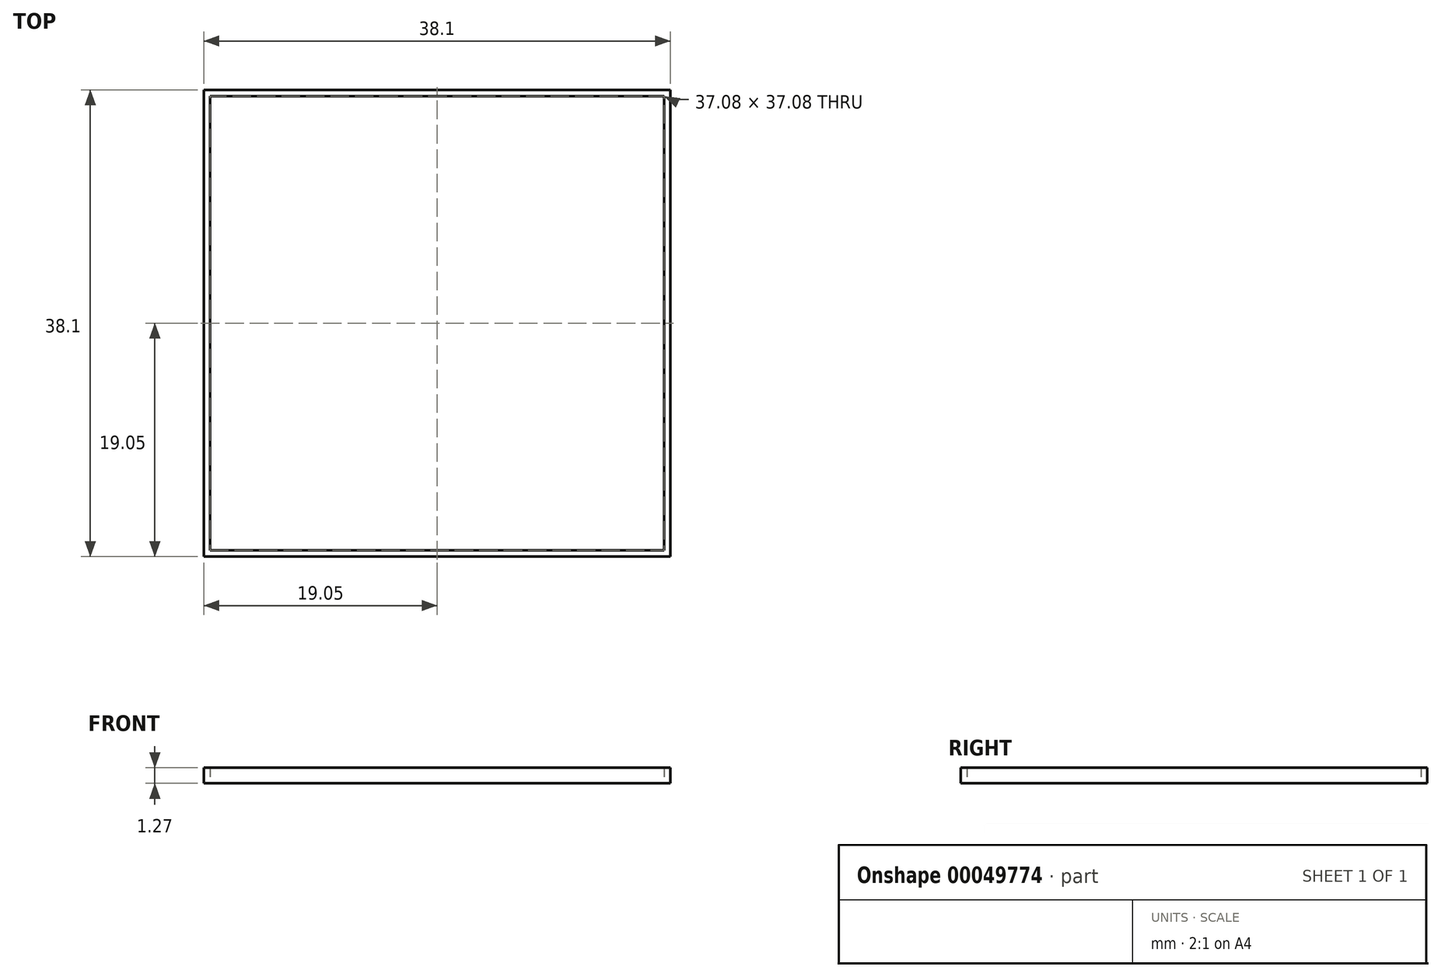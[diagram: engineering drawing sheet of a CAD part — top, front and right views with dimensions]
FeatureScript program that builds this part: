
annotation { "Feature Type Name" : "Feature", "Feature Type Description" : "" }
export const myFeature = defineFeature(function(context is Context, id is Id, definition is map)
    precondition{}
    {
        {
            var Q0;
            Q0=qCreatedBy(makeId("Top.planeOp"),FACE);
            var sketch = newSketch(context, id + "F0", { "sketchPlane" : qUnion([Q0])});
            skLineSegment(sketch, "E0.rect.bottom", {"start": v(19.05, -19.05) * mm, "end": v(-19.05, -19.05) * mm});
            skLineSegment(sketch, "E0.rect.top", {"start": v(19.05, 19.05) * mm, "end": v(-19.05, 19.05) * mm});
            skLineSegment(sketch, "E0.rect.left", {"start": v(19.05, -19.05) * mm, "end": v(19.05, 19.05) * mm});
            skLineSegment(sketch, "E0.rect.right", {"start": v(-19.05, -19.05) * mm, "end": v(-19.05, 19.05) * mm});
            skPoint(sketch, "E0.rect.middle", {"position": v(0, 0) * mm});
            skLineSegment(sketch, "E1.1.0.0", {"start": v(-18.54, -19.05) * mm, "end": v(-18.54, 19.05) * mm});
            skLineSegment(sketch, "E1.2.0.0", {"start": v(-18.03, -19.05) * mm, "end": v(-18.03, 19.05) * mm});
            skLineSegment(sketch, "E1.3.0.0", {"start": v(-17.53, -19.05) * mm, "end": v(-17.53, 19.05) * mm});
            skLineSegment(sketch, "E1.4.0.0", {"start": v(-17.02, -19.05) * mm, "end": v(-17.02, 19.05) * mm});
            skLineSegment(sketch, "E1.5.0.0", {"start": v(-16.5, -19.05) * mm, "end": v(-16.5, 19.05) * mm});
            skLineSegment(sketch, "E1.6.0.0", {"start": v(-16, -19.05) * mm, "end": v(-16, 19.05) * mm});
            skLineSegment(sketch, "E1.7.0.0", {"start": v(-15.5, -19.05) * mm, "end": v(-15.5, 19.05) * mm});
            skLineSegment(sketch, "E1.8.0.0", {"start": v(-14.99, -19.05) * mm, "end": v(-14.99, 19.05) * mm});
            skLineSegment(sketch, "E1.9.0.0", {"start": v(-14.48, -19.05) * mm, "end": v(-14.48, 19.05) * mm});
            skLineSegment(sketch, "E1.10.0.0", {"start": v(-13.97, -19.05) * mm, "end": v(-13.97, 19.05) * mm});
            skLineSegment(sketch, "E1.11.0.0", {"start": v(-13.46, -19.05) * mm, "end": v(-13.46, 19.05) * mm});
            skLineSegment(sketch, "E1.12.0.0", {"start": v(-12.95, -19.05) * mm, "end": v(-12.95, 19.05) * mm});
            skLineSegment(sketch, "E1.13.0.0", {"start": v(-12.45, -19.05) * mm, "end": v(-12.45, 19.05) * mm});
            skLineSegment(sketch, "E1.14.0.0", {"start": v(-11.94, -19.05) * mm, "end": v(-11.94, 19.05) * mm});
            skLineSegment(sketch, "E1.15.0.0", {"start": v(-11.43, -19.05) * mm, "end": v(-11.43, 19.05) * mm});
            skLineSegment(sketch, "E1.16.0.0", {"start": v(-10.92, -19.05) * mm, "end": v(-10.92, 19.05) * mm});
            skLineSegment(sketch, "E1.17.0.0", {"start": v(-10.41, -19.05) * mm, "end": v(-10.41, 19.05) * mm});
            skLineSegment(sketch, "E1.18.0.0", {"start": v(-9.9, -19.05) * mm, "end": v(-9.9, 19.05) * mm});
            skLineSegment(sketch, "E1.19.0.0", {"start": v(-9.4, -19.05) * mm, "end": v(-9.4, 19.05) * mm});
            skLineSegment(sketch, "E1.20.0.0", {"start": v(-8.89, -19.05) * mm, "end": v(-8.89, 19.05) * mm});
            skLineSegment(sketch, "E1.21.0.0", {"start": v(-8.38, -19.05) * mm, "end": v(-8.38, 19.05) * mm});
            skLineSegment(sketch, "E1.22.0.0", {"start": v(-7.87, -19.05) * mm, "end": v(-7.87, 19.05) * mm});
            skLineSegment(sketch, "E1.23.0.0", {"start": v(-7.37, -19.05) * mm, "end": v(-7.37, 19.05) * mm});
            skLineSegment(sketch, "E1.24.0.0", {"start": v(-6.86, -19.05) * mm, "end": v(-6.86, 19.05) * mm});
            skLineSegment(sketch, "E1.25.0.0", {"start": v(-6.35, -19.05) * mm, "end": v(-6.35, 19.05) * mm});
            skLineSegment(sketch, "E1.26.0.0", {"start": v(-5.84, -19.05) * mm, "end": v(-5.84, 19.05) * mm});
            skLineSegment(sketch, "E1.27.0.0", {"start": v(-5.33, -19.05) * mm, "end": v(-5.33, 19.05) * mm});
            skLineSegment(sketch, "E1.28.0.0", {"start": v(-4.83, -19.05) * mm, "end": v(-4.83, 19.05) * mm});
            skLineSegment(sketch, "E1.29.0.0", {"start": v(-4.32, -19.05) * mm, "end": v(-4.32, 19.05) * mm});
            skLineSegment(sketch, "E1.30.0.0", {"start": v(-3.8, -19.05) * mm, "end": v(-3.8, 19.05) * mm});
            skLineSegment(sketch, "E1.31.0.0", {"start": v(-3.3, -19.05) * mm, "end": v(-3.3, 19.05) * mm});
            skLineSegment(sketch, "E1.32.0.0", {"start": v(-2.8, -19.05) * mm, "end": v(-2.8, 19.05) * mm});
            skLineSegment(sketch, "E1.33.0.0", {"start": v(-2.29, -19.05) * mm, "end": v(-2.29, 19.05) * mm});
            skLineSegment(sketch, "E1.34.0.0", {"start": v(-1.78, -19.05) * mm, "end": v(-1.78, 19.05) * mm});
            skLineSegment(sketch, "E1.35.0.0", {"start": v(-1.27, -19.05) * mm, "end": v(-1.27, 19.05) * mm});
            skLineSegment(sketch, "E1.36.0.0", {"start": v(-0.76, -19.05) * mm, "end": v(-0.76, 19.05) * mm});
            skLineSegment(sketch, "E1.37.0.0", {"start": v(-0.25, -19.05) * mm, "end": v(-0.25, 19.05) * mm});
            skLineSegment(sketch, "E1.38.0.0", {"start": v(0.25, -19.05) * mm, "end": v(0.25, 19.05) * mm});
            skLineSegment(sketch, "E1.39.0.0", {"start": v(0.76, -19.05) * mm, "end": v(0.76, 19.05) * mm});
            skLineSegment(sketch, "E1.40.0.0", {"start": v(1.27, -19.05) * mm, "end": v(1.27, 19.05) * mm});
            skLineSegment(sketch, "E1.41.0.0", {"start": v(1.78, -19.05) * mm, "end": v(1.78, 19.05) * mm});
            skLineSegment(sketch, "E1.42.0.0", {"start": v(2.29, -19.05) * mm, "end": v(2.29, 19.05) * mm});
            skLineSegment(sketch, "E1.43.0.0", {"start": v(2.8, -19.05) * mm, "end": v(2.8, 19.05) * mm});
            skLineSegment(sketch, "E1.44.0.0", {"start": v(3.3, -19.05) * mm, "end": v(3.3, 19.05) * mm});
            skLineSegment(sketch, "E1.45.0.0", {"start": v(3.81, -19.05) * mm, "end": v(3.81, 19.05) * mm});
            skLineSegment(sketch, "E1.46.0.0", {"start": v(4.32, -19.05) * mm, "end": v(4.32, 19.05) * mm});
            skLineSegment(sketch, "E1.47.0.0", {"start": v(4.83, -19.05) * mm, "end": v(4.83, 19.05) * mm});
            skLineSegment(sketch, "E1.48.0.0", {"start": v(5.33, -19.05) * mm, "end": v(5.33, 19.05) * mm});
            skLineSegment(sketch, "E1.49.0.0", {"start": v(5.84, -19.05) * mm, "end": v(5.84, 19.05) * mm});
            skLineSegment(sketch, "E1.50.0.0", {"start": v(6.35, -19.05) * mm, "end": v(6.35, 19.05) * mm});
            skLineSegment(sketch, "E1.51.0.0", {"start": v(6.86, -19.05) * mm, "end": v(6.86, 19.05) * mm});
            skLineSegment(sketch, "E1.52.0.0", {"start": v(7.37, -19.05) * mm, "end": v(7.37, 19.05) * mm});
            skLineSegment(sketch, "E1.53.0.0", {"start": v(7.87, -19.05) * mm, "end": v(7.87, 19.05) * mm});
            skLineSegment(sketch, "E1.54.0.0", {"start": v(8.38, -19.05) * mm, "end": v(8.38, 19.05) * mm});
            skLineSegment(sketch, "E1.55.0.0", {"start": v(8.9, -19.05) * mm, "end": v(8.9, 19.05) * mm});
            skLineSegment(sketch, "E1.56.0.0", {"start": v(9.4, -19.05) * mm, "end": v(9.4, 19.05) * mm});
            skLineSegment(sketch, "E1.57.0.0", {"start": v(9.9, -19.05) * mm, "end": v(9.9, 19.05) * mm});
            skLineSegment(sketch, "E1.58.0.0", {"start": v(10.41, -19.05) * mm, "end": v(10.41, 19.05) * mm});
            skLineSegment(sketch, "E1.59.0.0", {"start": v(10.92, -19.05) * mm, "end": v(10.92, 19.05) * mm});
            skLineSegment(sketch, "E1.60.0.0", {"start": v(11.43, -19.05) * mm, "end": v(11.43, 19.05) * mm});
            skLineSegment(sketch, "E1.61.0.0", {"start": v(11.94, -19.05) * mm, "end": v(11.94, 19.05) * mm});
            skLineSegment(sketch, "E1.62.0.0", {"start": v(12.45, -19.05) * mm, "end": v(12.45, 19.05) * mm});
            skLineSegment(sketch, "E1.63.0.0", {"start": v(12.95, -19.05) * mm, "end": v(12.95, 19.05) * mm});
            skLineSegment(sketch, "E1.64.0.0", {"start": v(13.46, -19.05) * mm, "end": v(13.46, 19.05) * mm});
            skLineSegment(sketch, "E1.65.0.0", {"start": v(13.97, -19.05) * mm, "end": v(13.97, 19.05) * mm});
            skLineSegment(sketch, "E1.66.0.0", {"start": v(14.48, -19.05) * mm, "end": v(14.48, 19.05) * mm});
            skLineSegment(sketch, "E1.67.0.0", {"start": v(14.99, -19.05) * mm, "end": v(14.99, 19.05) * mm});
            skLineSegment(sketch, "E1.68.0.0", {"start": v(15.5, -19.05) * mm, "end": v(15.5, 19.05) * mm});
            skLineSegment(sketch, "E1.69.0.0", {"start": v(16, -19.05) * mm, "end": v(16, 19.05) * mm});
            skLineSegment(sketch, "E1.70.0.0", {"start": v(16.51, -19.05) * mm, "end": v(16.51, 19.05) * mm});
            skLineSegment(sketch, "E1.71.0.0", {"start": v(17.02, -19.05) * mm, "end": v(17.02, 19.05) * mm});
            skLineSegment(sketch, "E1.72.0.0", {"start": v(17.53, -19.05) * mm, "end": v(17.53, 19.05) * mm});
            skLineSegment(sketch, "E1.73.0.0", {"start": v(18.03, -19.05) * mm, "end": v(18.03, 19.05) * mm});
            skLineSegment(sketch, "E1.74.0.0", {"start": v(18.54, -19.05) * mm, "end": v(18.54, 19.05) * mm});
            skLineSegment(sketch, "E1.direction1", {"start": v(-19.05, -19.05) * mm, "end": v(-18.54, -19.05) * mm, "construction": true});
            skLineSegment(sketch, "E2.0.1.0", {"start": v(19.05, -18.54) * mm, "end": v(-18.54, -18.54) * mm});
            skLineSegment(sketch, "E2.0.2.0", {"start": v(19.05, -18.03) * mm, "end": v(-18.54, -18.03) * mm});
            skLineSegment(sketch, "E2.0.3.0", {"start": v(19.05, -17.53) * mm, "end": v(-18.54, -17.53) * mm});
            skLineSegment(sketch, "E2.0.4.0", {"start": v(19.05, -17.02) * mm, "end": v(-19.05, -17.02) * mm});
            skLineSegment(sketch, "E2.0.5.0", {"start": v(19.05, -16.5) * mm, "end": v(-19.05, -16.51) * mm});
            skLineSegment(sketch, "E2.0.6.0", {"start": v(19.05, -16) * mm, "end": v(-19.05, -16) * mm});
            skLineSegment(sketch, "E2.0.7.0", {"start": v(19.05, -15.5) * mm, "end": v(-19.05, -15.5) * mm});
            skLineSegment(sketch, "E2.0.8.0", {"start": v(19.05, -14.99) * mm, "end": v(-19.05, -14.99) * mm});
            skLineSegment(sketch, "E2.0.9.0", {"start": v(19.05, -14.48) * mm, "end": v(-19.05, -14.48) * mm});
            skLineSegment(sketch, "E2.0.10.0", {"start": v(19.05, -13.97) * mm, "end": v(-19.05, -13.97) * mm});
            skLineSegment(sketch, "E2.0.11.0", {"start": v(19.05, -13.46) * mm, "end": v(-19.05, -13.46) * mm});
            skLineSegment(sketch, "E2.0.12.0", {"start": v(19.05, -12.95) * mm, "end": v(-19.05, -12.95) * mm});
            skLineSegment(sketch, "E2.0.13.0", {"start": v(19.05, -12.45) * mm, "end": v(-19.05, -12.45) * mm});
            skLineSegment(sketch, "E2.0.14.0", {"start": v(19.05, -11.94) * mm, "end": v(-19.05, -11.94) * mm});
            skLineSegment(sketch, "E2.0.15.0", {"start": v(19.05, -11.43) * mm, "end": v(-19.05, -11.43) * mm});
            skLineSegment(sketch, "E2.0.16.0", {"start": v(19.05, -10.92) * mm, "end": v(-19.05, -10.92) * mm});
            skLineSegment(sketch, "E2.0.17.0", {"start": v(19.05, -10.41) * mm, "end": v(-19.05, -10.41) * mm});
            skLineSegment(sketch, "E2.0.18.0", {"start": v(19.05, -9.9) * mm, "end": v(-19.05, -9.9) * mm});
            skLineSegment(sketch, "E2.0.19.0", {"start": v(19.05, -9.4) * mm, "end": v(-19.05, -9.4) * mm});
            skLineSegment(sketch, "E2.0.20.0", {"start": v(19.05, -8.89) * mm, "end": v(-19.05, -8.89) * mm});
            skLineSegment(sketch, "E2.0.21.0", {"start": v(19.05, -8.38) * mm, "end": v(-19.05, -8.38) * mm});
            skLineSegment(sketch, "E2.0.22.0", {"start": v(19.05, -7.87) * mm, "end": v(-19.05, -7.87) * mm});
            skLineSegment(sketch, "E2.0.23.0", {"start": v(19.05, -7.37) * mm, "end": v(-19.05, -7.37) * mm});
            skLineSegment(sketch, "E2.0.24.0", {"start": v(19.05, -6.86) * mm, "end": v(-19.05, -6.86) * mm});
            skLineSegment(sketch, "E2.0.25.0", {"start": v(19.05, -6.35) * mm, "end": v(-19.05, -6.35) * mm});
            skLineSegment(sketch, "E2.0.26.0", {"start": v(19.05, -5.84) * mm, "end": v(-19.05, -5.84) * mm});
            skLineSegment(sketch, "E2.0.27.0", {"start": v(19.05, -5.33) * mm, "end": v(-19.05, -5.33) * mm});
            skLineSegment(sketch, "E2.0.28.0", {"start": v(19.05, -4.83) * mm, "end": v(-19.05, -4.83) * mm});
            skLineSegment(sketch, "E2.0.29.0", {"start": v(19.05, -4.32) * mm, "end": v(-19.05, -4.32) * mm});
            skLineSegment(sketch, "E2.0.30.0", {"start": v(19.05, -3.8) * mm, "end": v(-19.05, -3.8) * mm});
            skLineSegment(sketch, "E2.0.31.0", {"start": v(19.05, -3.3) * mm, "end": v(-19.05, -3.3) * mm});
            skLineSegment(sketch, "E2.0.32.0", {"start": v(19.05, -2.8) * mm, "end": v(-19.05, -2.8) * mm});
            skLineSegment(sketch, "E2.0.33.0", {"start": v(19.05, -2.29) * mm, "end": v(-19.05, -2.29) * mm});
            skLineSegment(sketch, "E2.0.34.0", {"start": v(19.05, -1.78) * mm, "end": v(-19.05, -1.78) * mm});
            skLineSegment(sketch, "E2.0.35.0", {"start": v(19.05, -1.27) * mm, "end": v(-19.05, -1.27) * mm});
            skLineSegment(sketch, "E2.0.36.0", {"start": v(19.05, -0.76) * mm, "end": v(-19.05, -0.76) * mm});
            skLineSegment(sketch, "E2.0.37.0", {"start": v(19.05, -0.25) * mm, "end": v(-19.05, -0.25) * mm});
            skLineSegment(sketch, "E2.0.38.0", {"start": v(19.05, 0.25) * mm, "end": v(-19.05, 0.25) * mm});
            skLineSegment(sketch, "E2.0.39.0", {"start": v(19.05, 0.76) * mm, "end": v(-19.05, 0.76) * mm});
            skLineSegment(sketch, "E2.0.40.0", {"start": v(19.05, 1.27) * mm, "end": v(-19.05, 1.27) * mm});
            skLineSegment(sketch, "E2.0.41.0", {"start": v(19.05, 1.78) * mm, "end": v(-19.05, 1.78) * mm});
            skLineSegment(sketch, "E2.0.42.0", {"start": v(19.05, 2.29) * mm, "end": v(-19.05, 2.29) * mm});
            skLineSegment(sketch, "E2.0.43.0", {"start": v(19.05, 2.8) * mm, "end": v(-19.05, 2.8) * mm});
            skLineSegment(sketch, "E2.0.44.0", {"start": v(19.05, 3.3) * mm, "end": v(-19.05, 3.3) * mm});
            skLineSegment(sketch, "E2.0.45.0", {"start": v(19.05, 3.81) * mm, "end": v(-19.05, 3.81) * mm});
            skLineSegment(sketch, "E2.0.46.0", {"start": v(19.05, 4.32) * mm, "end": v(-19.05, 4.32) * mm});
            skLineSegment(sketch, "E2.0.47.0", {"start": v(19.05, 4.83) * mm, "end": v(-19.05, 4.83) * mm});
            skLineSegment(sketch, "E2.0.48.0", {"start": v(19.05, 5.33) * mm, "end": v(-19.05, 5.33) * mm});
            skLineSegment(sketch, "E2.0.49.0", {"start": v(19.05, 5.84) * mm, "end": v(-19.05, 5.84) * mm});
            skLineSegment(sketch, "E2.0.50.0", {"start": v(19.05, 6.35) * mm, "end": v(-19.05, 6.35) * mm});
            skLineSegment(sketch, "E2.0.51.0", {"start": v(19.05, 6.86) * mm, "end": v(-19.05, 6.86) * mm});
            skLineSegment(sketch, "E2.0.52.0", {"start": v(19.05, 7.37) * mm, "end": v(-19.05, 7.37) * mm});
            skLineSegment(sketch, "E2.0.53.0", {"start": v(19.05, 7.87) * mm, "end": v(-19.05, 7.87) * mm});
            skLineSegment(sketch, "E2.0.54.0", {"start": v(19.05, 8.38) * mm, "end": v(-19.05, 8.38) * mm});
            skLineSegment(sketch, "E2.0.55.0", {"start": v(19.05, 8.9) * mm, "end": v(-19.05, 8.9) * mm});
            skLineSegment(sketch, "E2.0.56.0", {"start": v(19.05, 9.4) * mm, "end": v(-19.05, 9.4) * mm});
            skLineSegment(sketch, "E2.0.57.0", {"start": v(19.05, 9.9) * mm, "end": v(-19.05, 9.9) * mm});
            skLineSegment(sketch, "E2.0.58.0", {"start": v(19.05, 10.41) * mm, "end": v(-19.05, 10.41) * mm});
            skLineSegment(sketch, "E2.0.59.0", {"start": v(19.05, 10.92) * mm, "end": v(-19.05, 10.92) * mm});
            skLineSegment(sketch, "E2.0.60.0", {"start": v(19.05, 11.43) * mm, "end": v(-19.05, 11.43) * mm});
            skLineSegment(sketch, "E2.0.61.0", {"start": v(19.05, 11.94) * mm, "end": v(-19.05, 11.94) * mm});
            skLineSegment(sketch, "E2.0.62.0", {"start": v(19.05, 12.45) * mm, "end": v(-19.05, 12.45) * mm});
            skLineSegment(sketch, "E2.0.63.0", {"start": v(19.05, 12.95) * mm, "end": v(-19.05, 12.95) * mm});
            skLineSegment(sketch, "E2.0.64.0", {"start": v(19.05, 13.46) * mm, "end": v(-19.05, 13.46) * mm});
            skLineSegment(sketch, "E2.0.65.0", {"start": v(19.05, 13.97) * mm, "end": v(-19.05, 13.97) * mm});
            skLineSegment(sketch, "E2.0.66.0", {"start": v(19.05, 14.48) * mm, "end": v(-19.05, 14.48) * mm});
            skLineSegment(sketch, "E2.0.67.0", {"start": v(19.05, 14.99) * mm, "end": v(-19.05, 14.99) * mm});
            skLineSegment(sketch, "E2.0.68.0", {"start": v(19.05, 15.5) * mm, "end": v(-19.05, 15.5) * mm});
            skLineSegment(sketch, "E2.0.69.0", {"start": v(19.05, 16) * mm, "end": v(-19.05, 16) * mm});
            skLineSegment(sketch, "E2.0.70.0", {"start": v(19.05, 16.51) * mm, "end": v(-19.05, 16.51) * mm});
            skLineSegment(sketch, "E2.0.71.0", {"start": v(19.05, 17.02) * mm, "end": v(-19.05, 17.02) * mm});
            skLineSegment(sketch, "E2.0.72.0", {"start": v(19.05, 17.53) * mm, "end": v(-19.05, 17.53) * mm});
            skLineSegment(sketch, "E2.0.73.0", {"start": v(19.05, 18.03) * mm, "end": v(-19.05, 18.03) * mm});
            skLineSegment(sketch, "E2.0.74.0", {"start": v(19.05, 18.54) * mm, "end": v(-19.05, 18.54) * mm});
            skLineSegment(sketch, "E2.direction1", {"start": v(-19.05, -19.05) * mm, "end": v(19.05, -19.05) * mm, "construction": true});
            skLineSegment(sketch, "E2.direction2", {"start": v(-19.05, -19.05) * mm, "end": v(-19.05, -18.54) * mm, "construction": true});
            skLineSegment(sketch, "E3", {"start": v(-18.54, -18.54) * mm, "end": v(-19.05, -18.54) * mm});
            skLineSegment(sketch, "E4", {"start": v(-18.54, -18.03) * mm, "end": v(-19.05, -18.03) * mm});
            skLineSegment(sketch, "E5", {"start": v(-18.54, -17.53) * mm, "end": v(-19.05, -17.53) * mm});
            skSolve(sketch);
        }
        {
            var Q0;
            Q0=qSketchRegion(id+"F0",true);
            extrude(context, id + "F1", {"entities" : qUnion([Q0]), "depth" : 1.27 * mm});
        }
        {
            var Q0;
            Q0=qCreatedBy(makeId("Top.planeOp"),FACE);
            var sketch = newSketch(context, id + "F2", { "sketchPlane" : qUnion([Q0])});
            skCircle(sketch, "E6", {"center": v(13.97, 13.97) * mm, "radius": 1.59 * mm});
            skSolve(sketch);
        }
        {
            var Q0;
            Q0=qSketchRegion(id+"F2",true);
            extrude(context, id + "F3", {"entities" : qUnion([Q0]), "operationType" : NewBodyOperationType.REMOVE, "depth" : 25.4 * mm});
        }
        {
            var Q0;
            Q0=makeQuery(id+"F1.opExtrude","SWEPT_BODY",BODY,{"disambiguationData":[OSD([sQuery(id+"F0.wireOp",EDGE,"E0.rect.bottom"),sQuery(id+"F0.wireOp",EDGE,"E0.rect.top"),sQuery(id+"F0.wireOp",EDGE,"E0.rect.left"),sQuery(id+"F0.wireOp",EDGE,"E0.rect.right")])]});
            var Q1;
            Q1=qCreatedBy(makeId("Right.planeOp"),FACE);
            mirror(context, id + "F4", {"operationType" : NewBodyOperationType.INTERSECT, "entities" : qUnion([Q0]), "mirrorPlane" : qUnion([Q1])});
        }
        {
            var Q0;
            Q0=makeQuery(id+"F1.opExtrude","SWEPT_BODY",BODY,{"disambiguationData":[OSD([sQuery(id+"F0.wireOp",EDGE,"E0.rect.bottom"),sQuery(id+"F0.wireOp",EDGE,"E0.rect.top"),sQuery(id+"F0.wireOp",EDGE,"E0.rect.left"),sQuery(id+"F0.wireOp",EDGE,"E0.rect.right")])]});
            var Q1;
            Q1=qCreatedBy(makeId("Front.planeOp"),FACE);
            mirror(context, id + "F5", {"operationType" : NewBodyOperationType.INTERSECT, "entities" : qUnion([Q0]), "mirrorPlane" : qUnion([Q1])});
        }
    });
